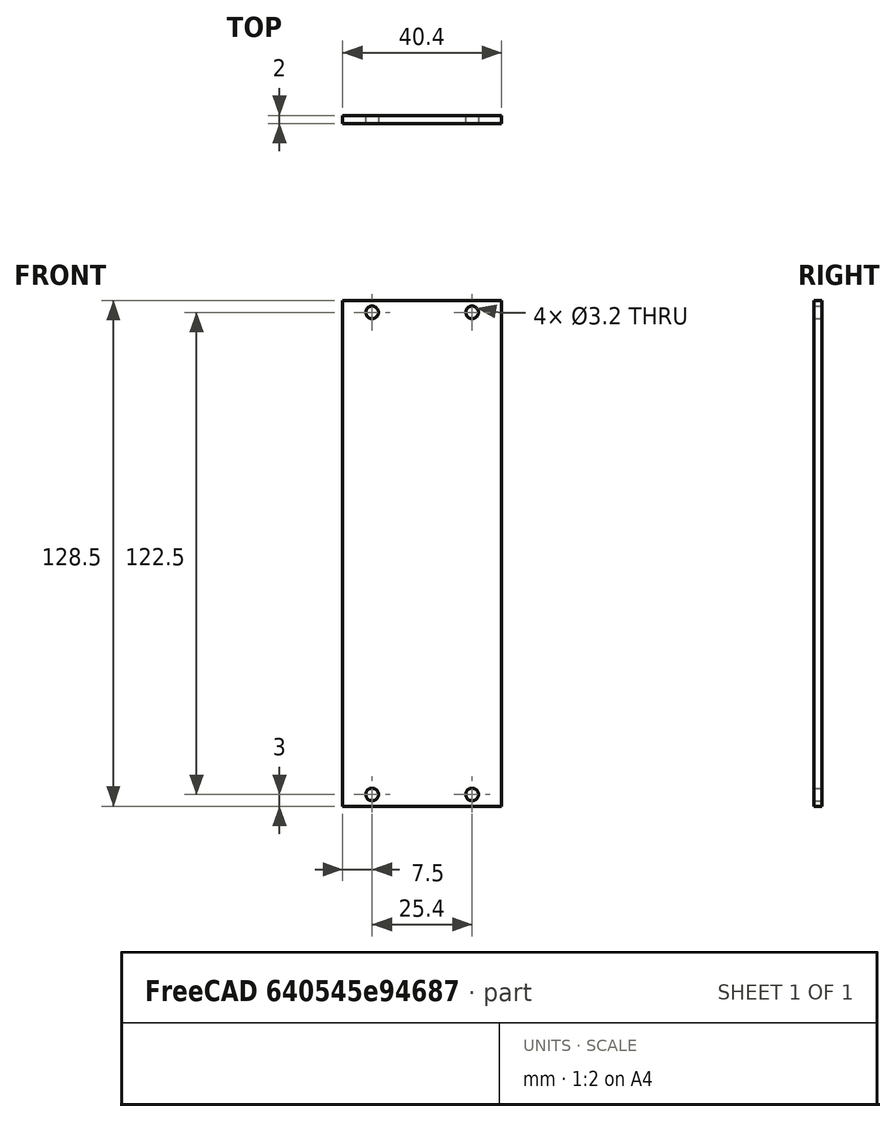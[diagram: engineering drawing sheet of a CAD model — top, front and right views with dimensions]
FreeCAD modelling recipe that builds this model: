
FCSTD DOCUMENT  (FreeCAD 1.0R38641 +468 (Git))
Label: 8hp_plate
License: All rights reserved
LicenseURL: https://en.wikipedia.org/wiki/All_rights_reserved
objects: Sketcher::SketchObject×1, PartDesign::Pad×1, PartDesign::Body×1, App::VarSet×1
note: 6 computed .brp shape members not serialized (recipe doc carries the construction recipe); baked Part::Feature solids carry a one-line shape summary decoded from their .brp
EXTERNAL_REF file=plate_dims.FCStd obj=VarSet

FEATURE [Sketcher::SketchObject] Sketch
  ArcFitTolerance = 1e-06
  AttachmentSupport = -> [XZ_Plane]
  FullyConstrained = true
  MakeInternals = false
  MapMode = 5
  Placement = pos=(0,0,0) rot=(1,0,0;1.5708rad)
  expr: Constraints[39] = <<plate_dims>>#VarSet.HoleOffsetY
  expr: Constraints[40] = <<plate_dims>>#VarSet.HoleOffsetX
  expr: Constraints[48] = <<plate_dims>>#VarSet.HoleDiameter
  expr: Constraints[49] = <<plate_dims>>#VarSet.PlateHeight
  expr: Constraints[52] = <<plate_dims>>#VarSet.HoleSpacing * (VarSet.PlateWidthHP - 3)
  sketch-geometry (20):
    g0: LineSegment StartX=-20.2 StartY=64.25 StartZ=0 EndX=-20.2 EndY=-64.25 EndZ=0
    g1: LineSegment StartX=-20.2 StartY=-64.25 StartZ=0 EndX=20.2 EndY=-64.25 EndZ=0
    g2: LineSegment StartX=20.2 StartY=-64.25 StartZ=0 EndX=20.2 EndY=64.25 EndZ=0
    g3: LineSegment StartX=20.2 StartY=64.25 StartZ=0 EndX=-20.2 EndY=64.25 EndZ=0
    g4: LineSegment [constr] StartX=12.7 StartY=61.25 StartZ=0 EndX=20.2 EndY=61.25 EndZ=0
    g5: LineSegment [constr] StartX=12.7 StartY=64.25 StartZ=0 EndX=12.7 EndY=61.25 EndZ=0
    g6: LineSegment [constr] StartX=12.7 StartY=61.25 StartZ=0 EndX=12.7 EndY=-61.25 EndZ=0
    g7: LineSegment [constr] StartX=12.7 StartY=-61.25 StartZ=0 EndX=12.7 EndY=-64.25 EndZ=0
    g8: LineSegment [constr] StartX=12.7 StartY=-61.25 StartZ=0 EndX=20.2 EndY=-61.25 EndZ=0
    g9: LineSegment [constr] StartX=-12.7 StartY=-61.25 StartZ=0 EndX=-12.7 EndY=-64.25 EndZ=0
    g10: LineSegment [constr] StartX=-20.2 StartY=-61.25 StartZ=0 EndX=-12.7 EndY=-61.25 EndZ=0
    g11: LineSegment [constr] StartX=-12.7 StartY=-61.25 StartZ=0 EndX=12.7 EndY=-61.25 EndZ=0
    g12: LineSegment [constr] StartX=-20.2 StartY=61.25 StartZ=0 EndX=-12.7 EndY=61.25 EndZ=0
    g13: LineSegment [constr] StartX=-12.7 StartY=61.25 StartZ=0 EndX=12.7 EndY=61.25 EndZ=0
    g14: LineSegment [constr] StartX=-12.7 StartY=64.25 StartZ=0 EndX=-12.7 EndY=61.25 EndZ=0
    g15: LineSegment [constr] StartX=-12.7 StartY=61.25 StartZ=0 EndX=-12.7 EndY=-61.25 EndZ=0
    g16: Circle CenterX=-12.7 CenterY=61.25 CenterZ=0 NormalX=0 NormalY=0 NormalZ=1 AngleXU=0 Radius=1.6
    g17: Circle CenterX=12.7 CenterY=61.25 CenterZ=0 NormalX=0 NormalY=0 NormalZ=1 AngleXU=0 Radius=1.6
    g18: Circle CenterX=12.7 CenterY=-61.25 CenterZ=0 NormalX=0 NormalY=0 NormalZ=1 AngleXU=0 Radius=1.6
    g19: Circle CenterX=-12.7 CenterY=-61.25 CenterZ=0 NormalX=0 NormalY=0 NormalZ=1 AngleXU=0 Radius=1.6
  constraints (58):
    c: Coincident(g0,g1)
    c: Coincident(g1,g2)
    c: Coincident(g2,g3)
    c: Coincident(g3,g0)
    c: Vertical(g2)
    c: Horizontal(g1)
    c: PointOnObject(g14,g3)
    c: PointOnObject(g9,g1)
    c: PointOnObject(g12,g0)
    c: PointOnObject(g4,g2)
    c: PointOnObject(g10,g0)
    c: PointOnObject(g8,g2)
    c: PointOnObject(g5,g3)
    c: PointOnObject(g7,g1)
    c: Coincident(g13,g4)
    c: Horizontal(g4)
    c: Coincident(g5,g6)
    c: Vertical(g5)
    c: Coincident(g6,g7)
    c: Vertical(g6)
    c: Vertical(g7)
    c: Coincident(g11,g8)
    c: Horizontal(g8)
    c: Coincident(g15,g9)
    c: Vertical(g9)
    c: Coincident(g10,g11)
    c: Horizontal(g10)
    c: Horizontal(g11)
    c: Coincident(g12,g13)
    c: Horizontal(g12)
    c: Horizontal(g13)
    c: Coincident(g14,g15)
    c: Vertical(g14)
    c: Vertical(g15)
    c: Coincident(g12,g14)
    c: Coincident(g9,g10)
    c: Coincident(g8,g6)
    c: Coincident(g4,g5)
    c: Equal(g9,g14)
    c: Distance(g9,g9) = 3
    c: Distance(g10,g10) = 7.5
    c: Coincident(g16,g12)
    c: Coincident(g17,g4)
    c: Coincident(g18,g6)
    c: Coincident(g19,g9)
    c: Equal(g19,g18)
    c: Equal(g18,g17)
    c: Equal(g17,g16)
    c: Diameter(g16) = 3.2
    c: DistanceY(g0,g0) = 128.5
    c: Distance(g12,g9) = 125.5
    c: Distance(g14,g14) = 3
    c: Distance(g11,g11) = 25.4
    c: Distance(g1,g1) = 40.4
    c: Symmetric(g0,g2,g-2)
    c: Symmetric(g0,g0,g-1)
    c: Distance(g8,g8) = 7.5
    c: Equal(g8,g10)
FEATURE [PartDesign::Pad] Pad
  Direction = (0,-1,2e-16)
  Length = 2
  Length2 = 10
  Placement = pos=(0,0,0) rot=(1,0,0;1.5708rad)
  Profile = -> Sketch
  ReferenceAxis = -> Sketch [N_Axis]
  Refine = true
  Suppressed = false
  Type = 0
  expr: Length = <<plate_dims>>#VarSet.PlateThickness
FEATURE [PartDesign::Body] Body  label="8HpPlate"
  AllowCompound = false
  Group = -> [Sketch,Pad]
  Origin = -> Origin
  Tip = -> Pad
FEATURE [App::VarSet] VarSet
  PlateWidthHP = 8
